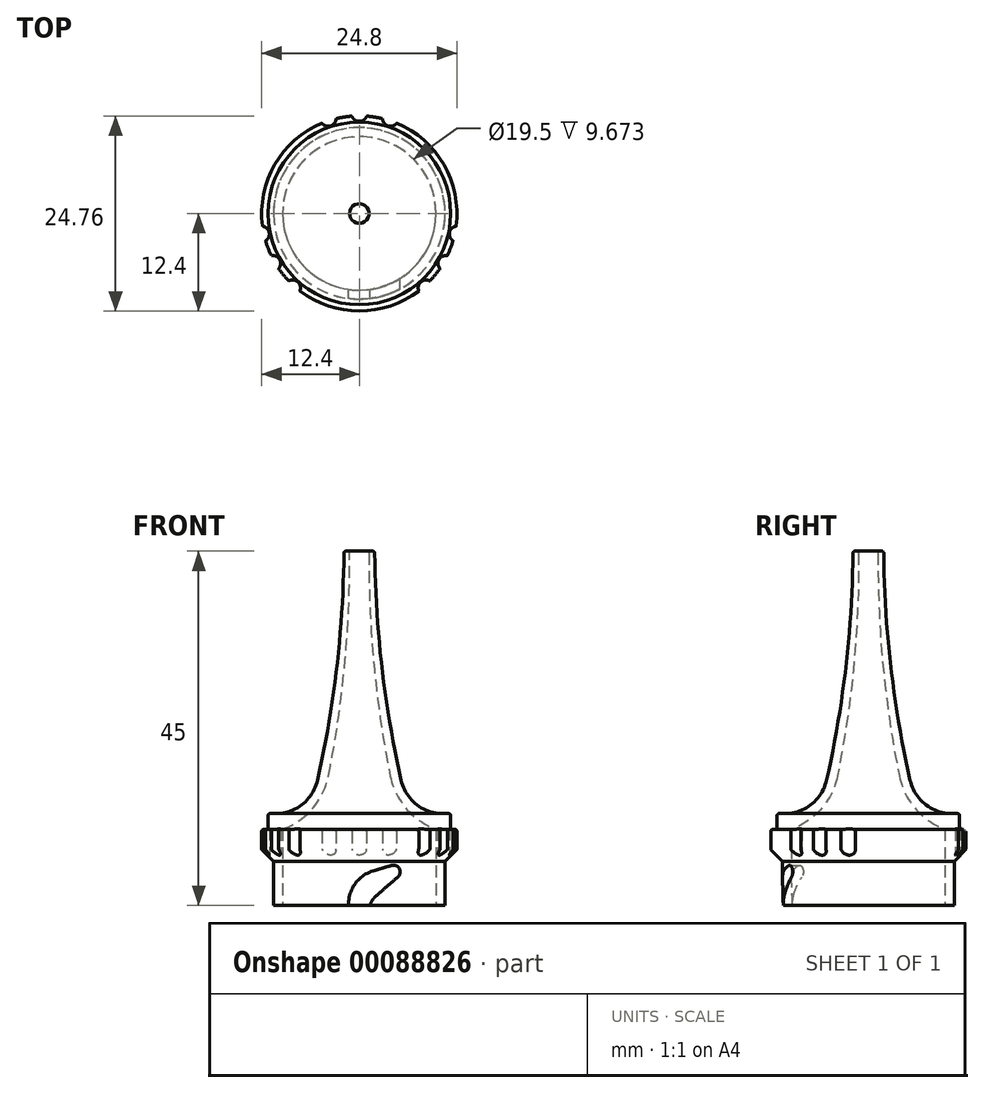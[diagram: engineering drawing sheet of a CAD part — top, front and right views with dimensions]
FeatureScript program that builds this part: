
annotation { "Feature Type Name" : "Feature", "Feature Type Description" : "" }
export const myFeature = defineFeature(function(context is Context, id is Id, definition is map)
    precondition{}
    {
        {
            var Q0;
            Q0=qCreatedBy(makeId("Front.planeOp"),FACE);
            var sketch = newSketch(context, id + "F0", { "sketchPlane" : qUnion([Q0])});
            skLineSegment(sketch, "E0", {"start": v(-10.6, 11.67) * mm, "end": v(-11.6, 11.67) * mm});
            skLineSegment(sketch, "E1", {"start": v(-11.6, 11.67) * mm, "end": v(-11.6, 9.67) * mm});
            skLineSegment(sketch, "E2", {"start": v(-11.6, 9.67) * mm, "end": v(-12.4, 9.67) * mm});
            skLineSegment(sketch, "E3", {"start": v(-12.4, 9.67) * mm, "end": v(-12.4, 7.07) * mm});
            skLineSegment(sketch, "E4", {"start": v(-12.4, 7.07) * mm, "end": v(-10.9, 5.57) * mm});
            skLineSegment(sketch, "E5", {"start": v(-10.9, 5.57) * mm, "end": v(-10.9, 0) * mm});
            skLineSegment(sketch, "E6", {"start": v(-10.9, 0) * mm, "end": v(-9.75, 0) * mm});
            skLineSegment(sketch, "E7", {"start": v(-9.75, 0) * mm, "end": v(-9.75, 9.67) * mm});
            skArc(sketch, "E8", {"start": v(-3.92, 16.47) * mm, "mid": v(-1.84, 30.67) * mm, "end": v(-1.25, 45) * mm});
            skLineSegment(sketch, "E9", {"start": v(-1.95, 45) * mm, "end": v(-1.25, 45) * mm});
            skArc(sketch, "E10", {"start": v(-10.6, 11.67) * mm, "mid": v(-7.21, 12.86) * mm, "end": v(-5.3, 15.9) * mm});
            skArc(sketch, "E11", {"start": v(-5.3, 15.9) * mm, "mid": v(-2.85, 30.36) * mm, "end": v(-1.95, 45) * mm});
            skArc(sketch, "E12", {"start": v(-9.75, 9.67) * mm, "mid": v(-5.95, 12.3) * mm, "end": v(-3.92, 16.47) * mm});
            skSolve(sketch);
        }
        {
            var Q0;
            Q0=qCreatedBy(makeId("Top.planeOp"),FACE);
            var sketch = newSketch(context, id + "F1", { "sketchPlane" : qUnion([Q0])});
            skCircle(sketch, "E13", {"center": v(0, 0) * mm, "radius": 22.52 * mm, "construction": true});
            skSolve(sketch);
        }
        {
            var Q0;
            Q0 = qSketchRegion(id + "F0", true);
            var Q1;
            Q1=sQuery(id+"F1.wireOp",EDGE,"E13");
            revolve(context, id + "F2", {"entities" : qUnion([Q0]), "axis" : qUnion([Q1]), "revolveType" : RevolveType.FULL});
        }
        {
            var Q0;
            Q0=makeQuery(id+"F2.opRevolve","SWEPT_EDGE",EDGE,{"disambiguationData":[OSD([sQuery(id+"F0.wireOp",EDGE,"E2"),sQuery(id+"F0.wireOp",EDGE,"E3")])]});
            var Q1;
            Q1=makeQuery(id+"F2.opRevolve","SWEPT_EDGE",EDGE,{"disambiguationData":[OSD([sQuery(id+"F0.wireOp",EDGE,"E3"),sQuery(id+"F0.wireOp",EDGE,"E4")])]});
            var Q2;
            Q2=makeQuery(id+"F2.opRevolve","SWEPT_EDGE",EDGE,{"disambiguationData":[OSD([sQuery(id+"F0.wireOp",EDGE,"E0"),sQuery(id+"F0.wireOp",EDGE,"E1")])]});
            var Q3;
            Q3=makeQuery(id+"F2.opRevolve","SWEPT_EDGE",EDGE,{"disambiguationData":[OSD([sQuery(id+"F0.wireOp",EDGE,"8GA3QGup-A811-RbUP-LmHQ-FKzoy5Im9zur"),sQuery(id+"F0.wireOp",EDGE,"E0")])]});
            var Q4;
            Q4=makeQuery(id+"F2.opRevolve","SWEPT_EDGE",EDGE,{"disambiguationData":[OSD([sQuery(id+"F0.wireOp",EDGE,"E1"),sQuery(id+"F0.wireOp",EDGE,"E2")])]});
            fillet(context, id + "F3", {"entities" : qUnion([Q0, Q1, Q2, Q3, Q4]), "radius" : 0.3 * mm, "tangentPropagation" : true, "allowEdgeOverflow" : false});
        }
        {
            var Q0;
            Q0=makeQuery(id+"F2.opRevolve","SWEPT_EDGE",EDGE,{"disambiguationData":[OSD([sQuery(id+"F0.wireOp",EDGE,"8GA3QGup-A811-RbUP-LmHQ-FKzoy5Im9zur"),sQuery(id+"F0.wireOp",EDGE,"E9")])]});
            var Q1;
            Q1=makeQuery(id+"F2.opRevolve","SWEPT_EDGE",EDGE,{"disambiguationData":[OSD([sQuery(id+"F0.wireOp",EDGE,"E8"),sQuery(id+"F0.wireOp",EDGE,"E9")])]});
            fillet(context, id + "F4", {"entities" : qUnion([Q0, Q1]), "radius" : 0.25 * mm, "tangentPropagation" : true, "allowEdgeOverflow" : false});
        }
        {
            var Q0;
            Q0=qCreatedBy(makeId("Top.planeOp"),FACE);
            var sketch = newSketch(context, id + "F5", { "sketchPlane" : qUnion([Q0])});
            skCircle(sketch, "E14", {"center": v(0, 12.7) * mm, "radius": 1 * mm});
            skCircle(sketch, "E15", {"center": v(-3.95, 12.07) * mm, "radius": 1 * mm});
            skCircle(sketch, "E16", {"center": v(3.95, 12.07) * mm, "radius": 1 * mm});
            skCircle(sketch, "E17", {"center": v(0, 0) * mm, "radius": 12.7 * mm, "construction": true});
            skCircle(sketch, "E18.1.0", {"center": v(-8.48, -9.46) * mm, "radius": 1 * mm});
            skCircle(sketch, "E18.1.1", {"center": v(-11, -6.35) * mm, "radius": 1 * mm});
            skCircle(sketch, "E18.1.2", {"center": v(-12.43, -2.61) * mm, "radius": 1 * mm});
            skCircle(sketch, "E18.2.0", {"center": v(12.43, -2.61) * mm, "radius": 1 * mm});
            skCircle(sketch, "E18.2.1", {"center": v(11, -6.35) * mm, "radius": 1 * mm});
            skCircle(sketch, "E18.2.2", {"center": v(8.48, -9.46) * mm, "radius": 1 * mm});
            skSolve(sketch);
        }
        {
            var Q0;
            Q0 = qSketchRegion(id + "F5", true);
            extrude(context, id + "F6", {"entities" : qUnion([Q0]), "operationType" : NewBodyOperationType.REMOVE, "depth" : 25 * mm});
        }
        {
            var Q0;
            Q0=qCreatedBy(makeId("Front.planeOp"),FACE);
            var sketch = newSketch(context, id + "F7", { "sketchPlane" : qUnion([Q0])});
            skLineSegment(sketch, "E19", {"start": v(-1.35, 0) * mm, "end": v(1.35, 0) * mm});
            skArc(sketch, "E20", {"start": v(2.11, 1.18) * mm, "mid": v(1.65, 0.64) * mm, "end": v(1.35, 0) * mm});
            skLineSegment(sketch, "E21", {"start": v(2.11, 1.18) * mm, "end": v(4.9, 3.62) * mm});
            skArc(sketch, "E22", {"start": v(4.9, 3.62) * mm, "mid": v(5.08, 4.67) * mm, "end": v(4.1, 5.07) * mm});
            skLineSegment(sketch, "E23", {"start": v(4.1, 5.07) * mm, "end": v(1.74, 4.37) * mm});
            skArc(sketch, "E24", {"start": v(1.74, 4.37) * mm, "mid": v(-0.56, 2.72) * mm, "end": v(-1.35, 0) * mm});
            skPoint(sketch, "E25", {"position": v(0, 0) * mm});
            skSolve(sketch);
        }
        {
            var Q0;
            Q0 = qSketchRegion(id + "F7", true);
            extrude(context, id + "F8", {"entities" : qUnion([Q0]), "operationType" : NewBodyOperationType.REMOVE, "depth" : 25 * mm});
        }
    });
